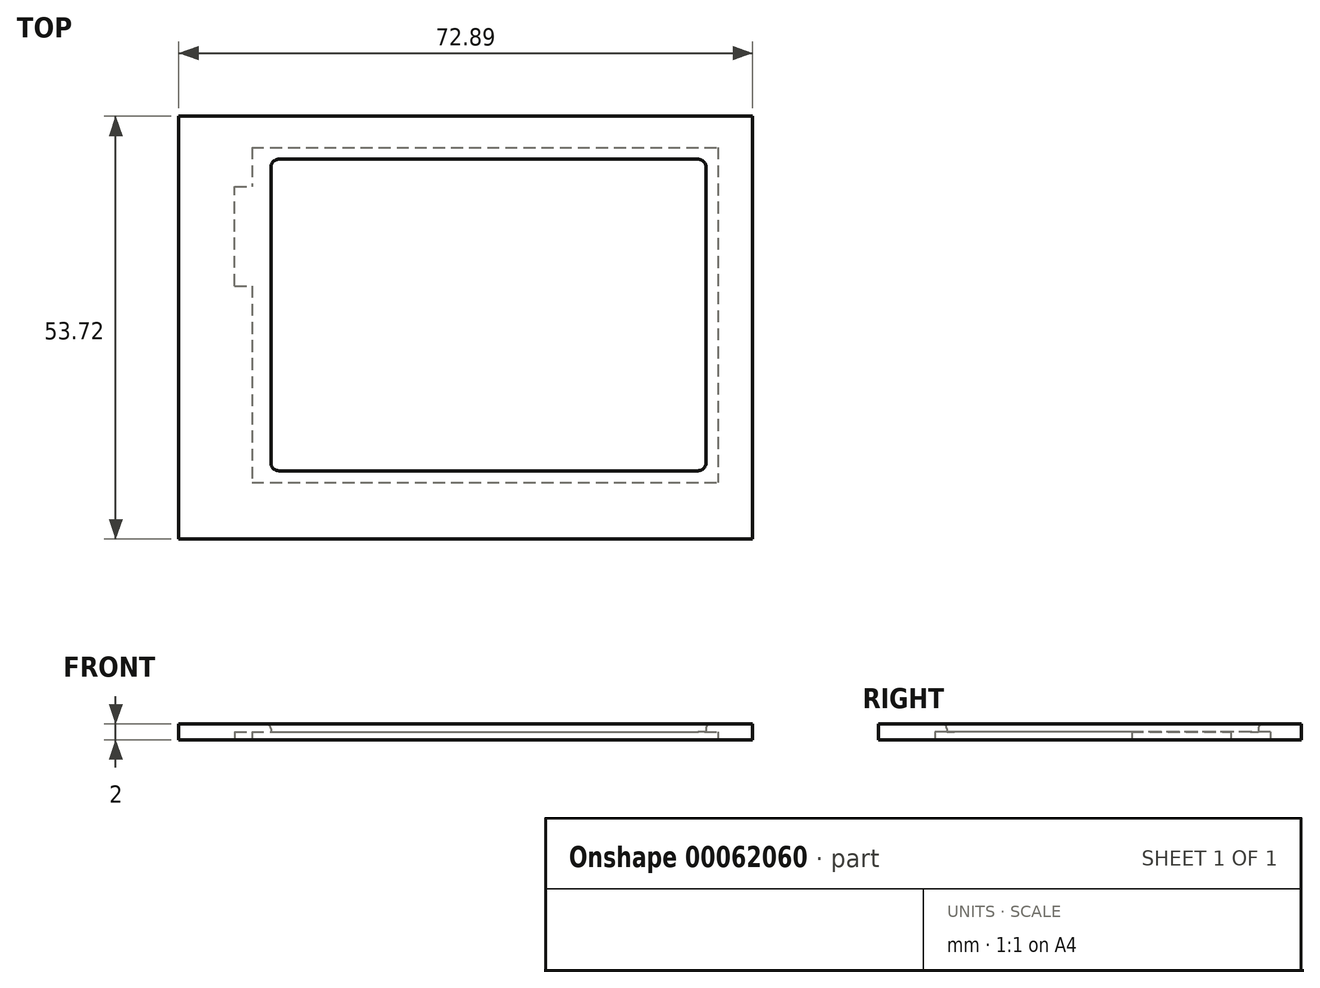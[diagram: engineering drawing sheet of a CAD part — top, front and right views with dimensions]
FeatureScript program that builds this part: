
annotation { "Feature Type Name" : "Feature", "Feature Type Description" : "" }
export const myFeature = defineFeature(function(context is Context, id is Id, definition is map)
    precondition{}
    {
        {
            var Q0;
            Q0=qCreatedBy(makeId("Top.planeOp"),FACE);
            var sketch = newSketch(context, id + "F0", { "sketchPlane" : qUnion([Q0])});
            skLineSegment(sketch, "E0.bottom", {"start": v(-30.83, 34.79) * mm, "end": v(42.06, 34.79) * mm});
            skLineSegment(sketch, "E0.top", {"start": v(-30.83, -18.93) * mm, "end": v(42.06, -18.93) * mm});
            skLineSegment(sketch, "E0.left", {"start": v(-30.83, 34.79) * mm, "end": v(-30.83, -18.93) * mm});
            skLineSegment(sketch, "E0.right", {"start": v(42.06, 34.79) * mm, "end": v(42.06, -18.93) * mm});
            skLineSegment(sketch, "E1", {"start": v(37.68, 30.82) * mm, "end": v(37.68, -11.76) * mm});
            skLineSegment(sketch, "E2", {"start": v(-21.53, -11.76) * mm, "end": v(37.68, -11.76) * mm});
            skLineSegment(sketch, "E3", {"start": v(-21.53, 30.82) * mm, "end": v(37.68, 30.82) * mm});
            skLineSegment(sketch, "E4", {"start": v(-21.53, 30.82) * mm, "end": v(-21.53, -11.76) * mm});
            skLineSegment(sketch, "E5.filletArc", {"start": v(37.68, 30.82) * mm, "end": v(37.68, 30.82) * mm});
            skLineSegment(sketch, "E6.filletArc", {"start": v(37.68, -11.76) * mm, "end": v(37.68, -11.76) * mm});
            skPoint(sketch, "E7.newPointA", {"position": v(-21.53, 30.82) * mm});
            skPoint(sketch, "E7.newPointB", {"position": v(-21.53, 29.79) * mm});
            skLineSegment(sketch, "E7.filletArc", {"start": v(-21.53, 30.82) * mm, "end": v(-21.53, 30.82) * mm});
            skLineSegment(sketch, "E8.filletArc", {"start": v(-21.53, -11.76) * mm, "end": v(-21.53, -11.76) * mm});
            skLineSegment(sketch, "E9.0", {"start": v(-18.13, 29.32) * mm, "end": v(35.13, 29.32) * mm});
            skLineSegment(sketch, "E10.0", {"start": v(36.13, 28.32) * mm, "end": v(36.13, -9.26) * mm});
            skLineSegment(sketch, "E11.0", {"start": v(-18.13, -10.26) * mm, "end": v(35.13, -10.26) * mm});
            skLineSegment(sketch, "E12.0", {"start": v(-19.13, 28.32) * mm, "end": v(-19.13, -9.26) * mm});
            skArc(sketch, "E13.filletArc", {"start": v(-18.13, 29.32) * mm, "mid": v(-18.84, 29.03) * mm, "end": v(-19.13, 28.32) * mm});
            skArc(sketch, "E14.filletArc", {"start": v(36.13, 28.32) * mm, "mid": v(35.84, 29.03) * mm, "end": v(35.13, 29.32) * mm});
            skArc(sketch, "E15.filletArc", {"start": v(35.13, -10.26) * mm, "mid": v(35.84, -9.97) * mm, "end": v(36.13, -9.26) * mm});
            skArc(sketch, "E16.filletArc", {"start": v(-19.13, -9.26) * mm, "mid": v(-18.84, -9.97) * mm, "end": v(-18.13, -10.26) * mm});
            skLineSegment(sketch, "E17.bottom", {"start": v(-23.73, 13.24) * mm, "end": v(-21.53, 13.24) * mm});
            skLineSegment(sketch, "E17.top", {"start": v(-23.73, 25.82) * mm, "end": v(-21.53, 25.82) * mm});
            skLineSegment(sketch, "E17.left", {"start": v(-23.73, 13.24) * mm, "end": v(-23.73, 25.82) * mm});
            skLineSegment(sketch, "E17.right", {"start": v(-21.53, 13.24) * mm, "end": v(-21.53, 25.82) * mm});
            skSolve(sketch);
        }
        {
            var Q0;
            Q0=makeQuery(id+"F0.imprint","IMPRINT",FACE,{"disambiguationData":[TD([[makeQuery(id+"F0.imprint","IMPRINT",EDGE,{"derivedFrom":sQuery(id+"F0.wireOp",EDGE,"E0.bottom")}),-1.0]])]});
            var Q1;
            Q1=makeQuery(id+"F0.imprint","IMPRINT",FACE,{"disambiguationData":[TD([[makeQuery(id+"F0.imprint","IMPRINT",EDGE,{"derivedFrom":sQuery(id+"F0.wireOp",EDGE,"E1")}),-1.0]])]});
            extrude(context, id + "F1", {"entities" : qUnion([Q0, Q1]), "depth" : 2 * mm});
        }
        {
            var Q0;
            Q0=makeQuery(id+"F0.imprint","IMPRINT",FACE,{"disambiguationData":[TD([[makeQuery(id+"F0.imprint","IMPRINT",EDGE,{"derivedFrom":sQuery(id+"F0.wireOp",EDGE,"E1")}),-1.0]])]});
            extrude(context, id + "F2", {"entities" : qUnion([Q0]), "operationType" : NewBodyOperationType.REMOVE, "depth" : 1 * mm});
        }
        {
            var Q0;
            Q0=makeQuery(id+"F0.imprint","IMPRINT",FACE,{"disambiguationData":[TD([[makeQuery(id+"F0.imprint","IMPRINT",EDGE,{"derivedFrom":sQuery(id+"F0.wireOp",EDGE,"E17.bottom")}),1.0]])]});
            extrude(context, id + "F3", {"entities" : qUnion([Q0]), "operationType" : NewBodyOperationType.ADD, "depth" : 2 * mm, "hasSecondDirection" : true, "secondDirectionOppositeDirection" : false, "secondDirectionDepth" : 1 * mm});
        }
        {
            var Q0;
            Q0=makeQuery(id+"F1.opExtrude","CAP_EDGE",EDGE,{"disambiguationData":[OSD([sQuery(id+"F0.wireOp",EDGE,"E9.0")])],"isStart":false});
            var Q1;
            Q1=makeQuery(id+"F1.opExtrude","CAP_EDGE",EDGE,{"disambiguationData":[OSD([sQuery(id+"F0.wireOp",EDGE,"E12.0")])],"isStart":false});
            var Q2;
            Q2=makeQuery(id+"F1.opExtrude","CAP_EDGE",EDGE,{"disambiguationData":[OSD([sQuery(id+"F0.wireOp",EDGE,"E11.0")])],"isStart":false});
            var Q3;
            Q3=makeQuery(id+"F1.opExtrude","CAP_EDGE",EDGE,{"disambiguationData":[OSD([sQuery(id+"F0.wireOp",EDGE,"E10.0")])],"isStart":false});
            fillet(context, id + "F4", {"entities" : qUnion([Q0, Q1, Q2, Q3]), "radius" : 0.6 * mm, "tangentPropagation" : true, "allowEdgeOverflow" : false});
        }
    });
